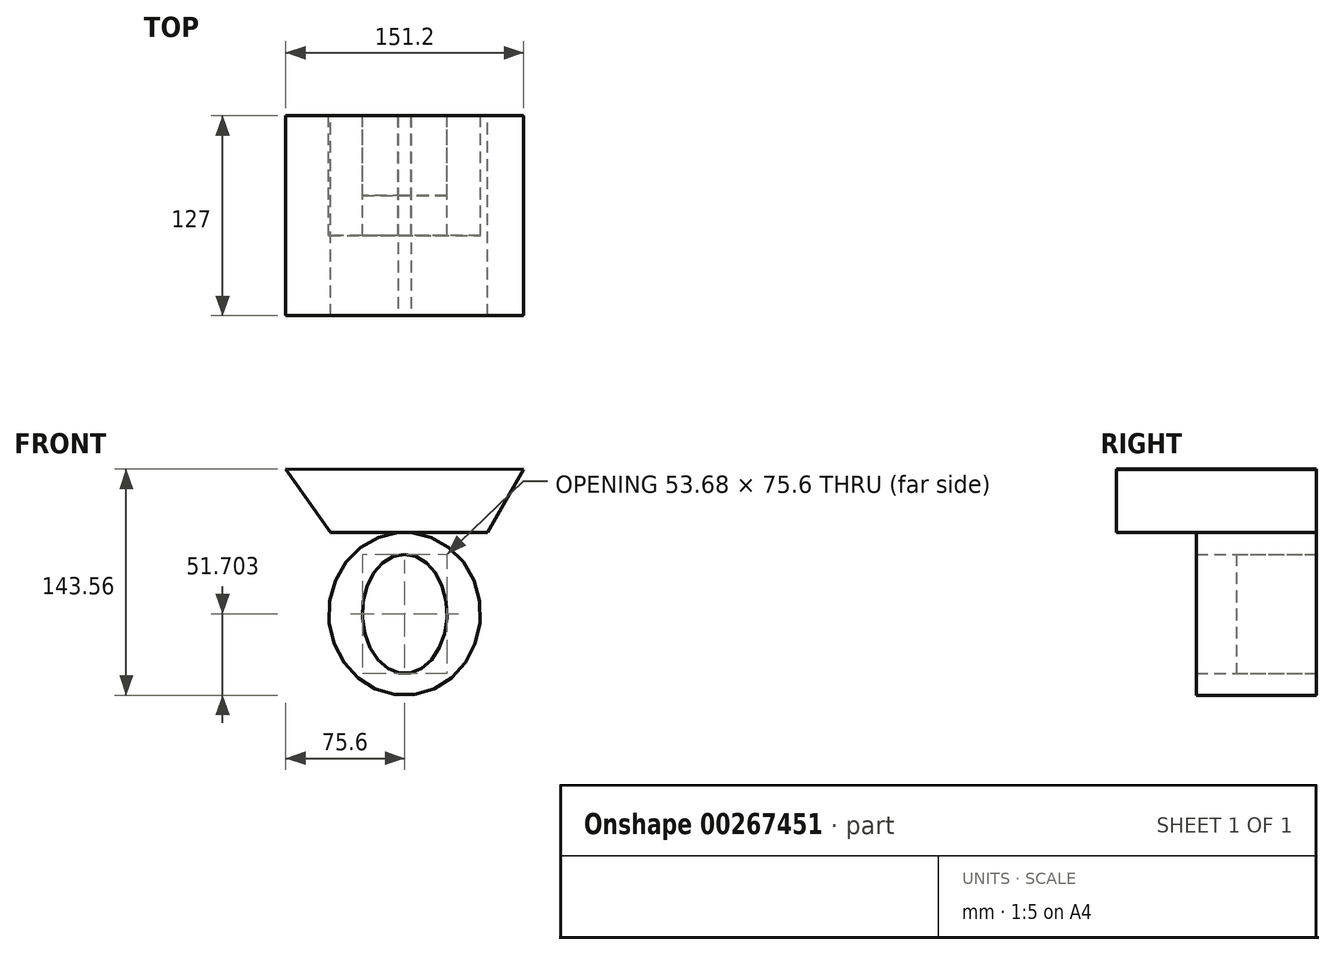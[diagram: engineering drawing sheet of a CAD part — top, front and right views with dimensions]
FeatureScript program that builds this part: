
annotation { "Feature Type Name" : "Feature", "Feature Type Description" : "" }
export const myFeature = defineFeature(function(context is Context, id is Id, definition is map)
    precondition{}
    {
        {
            var Q0;
            Q0=qCreatedBy(makeId("Front.planeOp"),FACE);
            var sketch = newSketch(context, id + "F0", { "sketchPlane" : qUnion([Q0])});
            skLineSegment(sketch, "E0", {"start": v(75.6, 75.9) * mm, "end": v(52.69, 35.74) * mm});
            skLineSegment(sketch, "E1", {"start": v(52.69, 35.74) * mm, "end": v(-47, 35.74) * mm});
            skLineSegment(sketch, "E2", {"start": v(-47, 35.74) * mm, "end": v(-75.6, 76.1) * mm});
            skLineSegment(sketch, "E3", {"start": v(-75.6, 76.1) * mm, "end": v(75.6, 75.9) * mm});
            skEllipse(sketch, "E4", {"center": v(0, -15.77) * mm, "majorRadius": 51.7 * mm, "minorRadius": 48.19 * mm, "majorAxis": v(0, 1)});
            skEllipse(sketch, "E5", {"center": v(0, -15.77) * mm, "majorRadius": 37.8 * mm, "minorRadius": 26.84 * mm, "majorAxis": v(0, 1)});
            skSolve(sketch);
        }
        {
            var Q0;
            {var subQ4=sQuery(id+"F0.wireOp",EDGE,"E0");Q0=makeQuery(id+"F0.imprint","IMPRINT",FACE,{"disambiguationData":[TD([[makeQuery(id+"F0.imprint","IMPRINT",EDGE,{"derivedFrom":subQ4}),-1.0]])]});}
            extrude(context, id + "F1", {"entities" : qUnion([Q0]), "depth" : 127 * mm});
        }
        {
            var Q0;
            Q0=makeQuery(id+"F0.imprint","IMPRINT",FACE,{"disambiguationData":[TD([[makeQuery(id+"F0.imprint","IMPRINT",EDGE,{"derivedFrom":sQuery(id+"F0.wireOp",EDGE,"E5")}),1.0]])]});
            extrude(context, id + "F2", {"entities" : qUnion([Q0]), "depth" : 50.8 * mm});
        }
        {
            var Q0;
            Q0=makeQuery(id+"F0.imprint","IMPRINT",FACE,{"disambiguationData":[TD([[makeQuery(id+"F0.imprint","IMPRINT",EDGE,{"derivedFrom":sQuery(id+"F0.wireOp",EDGE,"E5")}),-1.0]])]});
            extrude(context, id + "F3", {"entities" : qUnion([Q0]), "depth" : 76.2 * mm});
        }
    });
